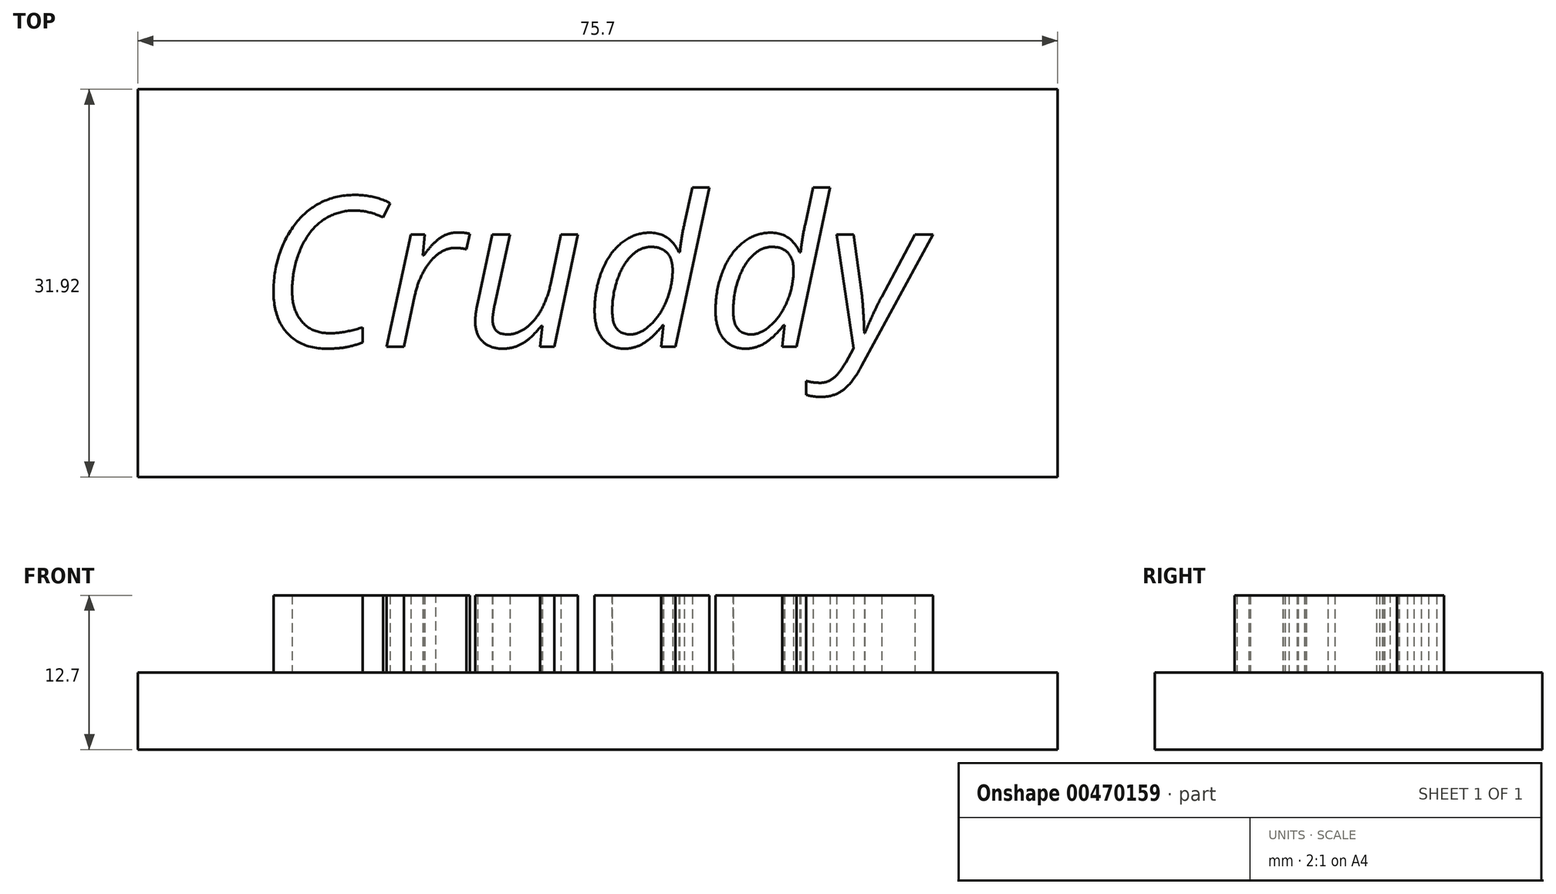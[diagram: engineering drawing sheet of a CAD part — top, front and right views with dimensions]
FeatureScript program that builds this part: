
annotation { "Feature Type Name" : "Feature", "Feature Type Description" : "" }
export const myFeature = defineFeature(function(context is Context, id is Id, definition is map)
    precondition{}
    {
        {
            var Q0;
            Q0=qCreatedBy(makeId("Top.planeOp"),FACE);
            var sketch = newSketch(context, id + "F0", { "sketchPlane" : qUnion([Q0])});
            skLineSegment(sketch, "E0.bottom", {"start": v(-37.85, 15.96) * mm, "end": v(37.85, 15.96) * mm});
            skLineSegment(sketch, "E0.top", {"start": v(-37.85, -15.96) * mm, "end": v(37.85, -15.96) * mm});
            skLineSegment(sketch, "E0.left", {"start": v(-37.85, 15.96) * mm, "end": v(-37.85, -15.96) * mm});
            skLineSegment(sketch, "E0.right", {"start": v(37.85, 15.96) * mm, "end": v(37.85, -15.96) * mm});
            skPoint(sketch, "E0.middle", {"position": v(0, 0) * mm});
            skSolve(sketch);
        }
        {
            var Q0;
            Q0=makeQuery(id+"F0.imprint","IMPRINT",FACE,{"disambiguationData":[TD([[makeQuery(id+"F0.imprint","IMPRINT",EDGE,{"derivedFrom":sQuery(id+"F0.wireOp",EDGE,"E0.bottom")}),-1.0]])]});
            extrude(context, id + "F1", {"entities" : qUnion([Q0]), "depth" : 6.35 * mm});
        }
        {
            var Q0;
            Q0=qCreatedBy(makeId("Top.planeOp"),FACE);
            var sketch = newSketch(context, id + "F2", { "sketchPlane" : qUnion([Q0])});
            skText(sketch, "E1", { "text": "Cruddy", "fontName": "OpenSans-Italic.ttf"});
            const initialGuessF2  = {"E1": [-0.02796, -0.00523, 1, 0, 0.01242]};
            skSetInitialGuess(sketch, initialGuessF2);
            skSolve(sketch);
        }
        {
            var Q0;
            Q0 = qSketchRegion(id + "F2", true);
            extrude(context, id + "F3", {"entities" : qUnion([Q0]), "operationType" : NewBodyOperationType.ADD, "depth" : 12.7 * mm});
        }
    });
